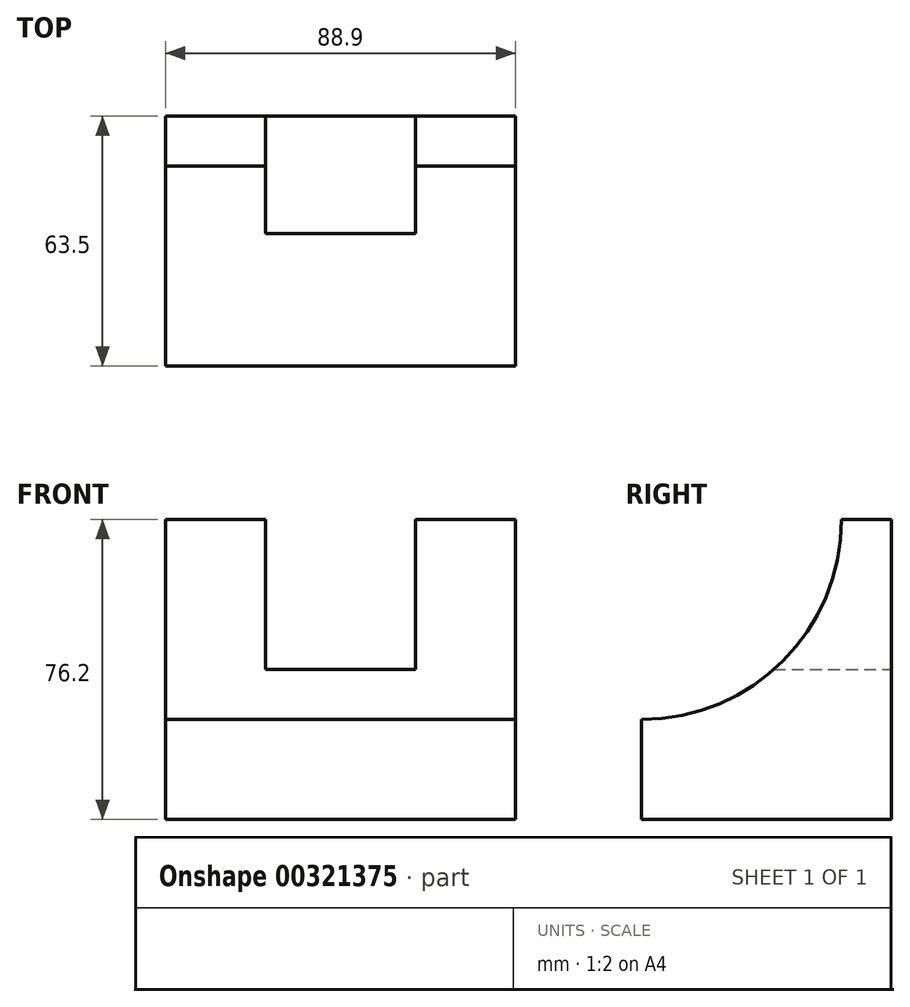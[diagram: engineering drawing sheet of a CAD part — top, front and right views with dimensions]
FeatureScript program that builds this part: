
annotation { "Feature Type Name" : "Feature", "Feature Type Description" : "" }
export const myFeature = defineFeature(function(context is Context, id is Id, definition is map)
    precondition{}
    {
        {
            var Q0;
            Q0=qCreatedBy(makeId("Front.planeOp"),FACE);
            var sketch = newSketch(context, id + "F0", { "sketchPlane" : qUnion([Q0])});
            skLineSegment(sketch, "E0.bottom", {"start": v(-42.05, 24.77) * mm, "end": v(46.85, 24.77) * mm});
            skLineSegment(sketch, "E0.top", {"start": v(-42.05, -51.43) * mm, "end": v(46.85, -51.43) * mm});
            skLineSegment(sketch, "E0.left", {"start": v(-42.05, 24.77) * mm, "end": v(-42.05, -51.43) * mm});
            skLineSegment(sketch, "E0.right", {"start": v(46.85, 24.77) * mm, "end": v(46.85, -51.43) * mm});
            skSolve(sketch);
        }
        {
            var Q0;
            Q0 = qSketchRegion(id + "F0", true);
            extrude(context, id + "F1", {"entities" : qUnion([Q0]), "depth" : 63.5 * mm});
        }
        {
            var Q0;
            Q0=makeQuery(id+"F1.opExtrude","CAP_FACE",FACE,{"disambiguationData":[OSD([sQuery(id+"F0.wireOp",EDGE,"E0.bottom"),sQuery(id+"F0.wireOp",EDGE,"E0.top"),sQuery(id+"F0.wireOp",EDGE,"E0.left"),sQuery(id+"F0.wireOp",EDGE,"E0.right")])],"isStart":true});
            var sketch = newSketch(context, id + "F2", { "sketchPlane" : qUnion([Q0])});
            skLineSegment(sketch, "E1", {"start": v(-46.85, 24.77) * mm, "end": v(-21.45, 24.77) * mm});
            skLineSegment(sketch, "E2", {"start": v(42.05, 24.77) * mm, "end": v(16.65, 24.77) * mm});
            skLineSegment(sketch, "E3", {"start": v(-21.45, 24.77) * mm, "end": v(-21.45, -13.33) * mm});
            skLineSegment(sketch, "E4", {"start": v(-21.45, -13.33) * mm, "end": v(16.65, -13.33) * mm});
            skLineSegment(sketch, "E5", {"start": v(16.65, -13.33) * mm, "end": v(16.65, 24.77) * mm});
            skSolve(sketch);
        }
        {
            var Q0;
            {var subQ0=sQuery(id+"F2.wireOp",EDGE,"E3");Q0=makeQuery(id+"F2.imprint","IMPRINT",FACE,{"disambiguationData":[TD([[makeQuery(id+"F2.imprint","IMPRINT",EDGE,{"derivedFrom":subQ0}),1.0]])]});}
            extrude(context, id + "F3", {"entities" : qUnion([Q0]), "operationType" : NewBodyOperationType.REMOVE, "endBound" : BoundingType.THROUGH_ALL, "oppositeDirection" : true, "depth" : 25.4 * mm});
        }
        {
            var Q0;
            Q0=makeQuery(id+"F1.opExtrude","SWEPT_FACE",FACE,{"disambiguationData":[OSD([sQuery(id+"F0.wireOp",EDGE,"E0.left")])]});
            var sketch = newSketch(context, id + "F4", { "sketchPlane" : qUnion([Q0])});
            skArc(sketch, "E6", {"start": v(12.7, 24.77) * mm, "mid": v(27.58, -11.15) * mm, "end": v(63.5, -26.03) * mm});
            skLineSegment(sketch, "E7", {"start": v(12.7, 24.77) * mm, "end": v(63.5, 24.77) * mm});
            skLineSegment(sketch, "E8", {"start": v(63.5, 24.77) * mm, "end": v(63.5, -26.03) * mm});
            skSolve(sketch);
        }
        {
            var Q0;
            Q0=makeQuery(id+"F4.imprint","IMPRINT",FACE,{"disambiguationData":[TD([[makeQuery(id+"F4.imprint","IMPRINT",EDGE,{"derivedFrom":sQuery(id+"F4.wireOp",EDGE,"E6")}),1.0]])]});
            extrude(context, id + "F5", {"entities" : qUnion([Q0]), "operationType" : NewBodyOperationType.REMOVE, "endBound" : BoundingType.THROUGH_ALL, "oppositeDirection" : true, "depth" : 25.4 * mm});
        }
    });
